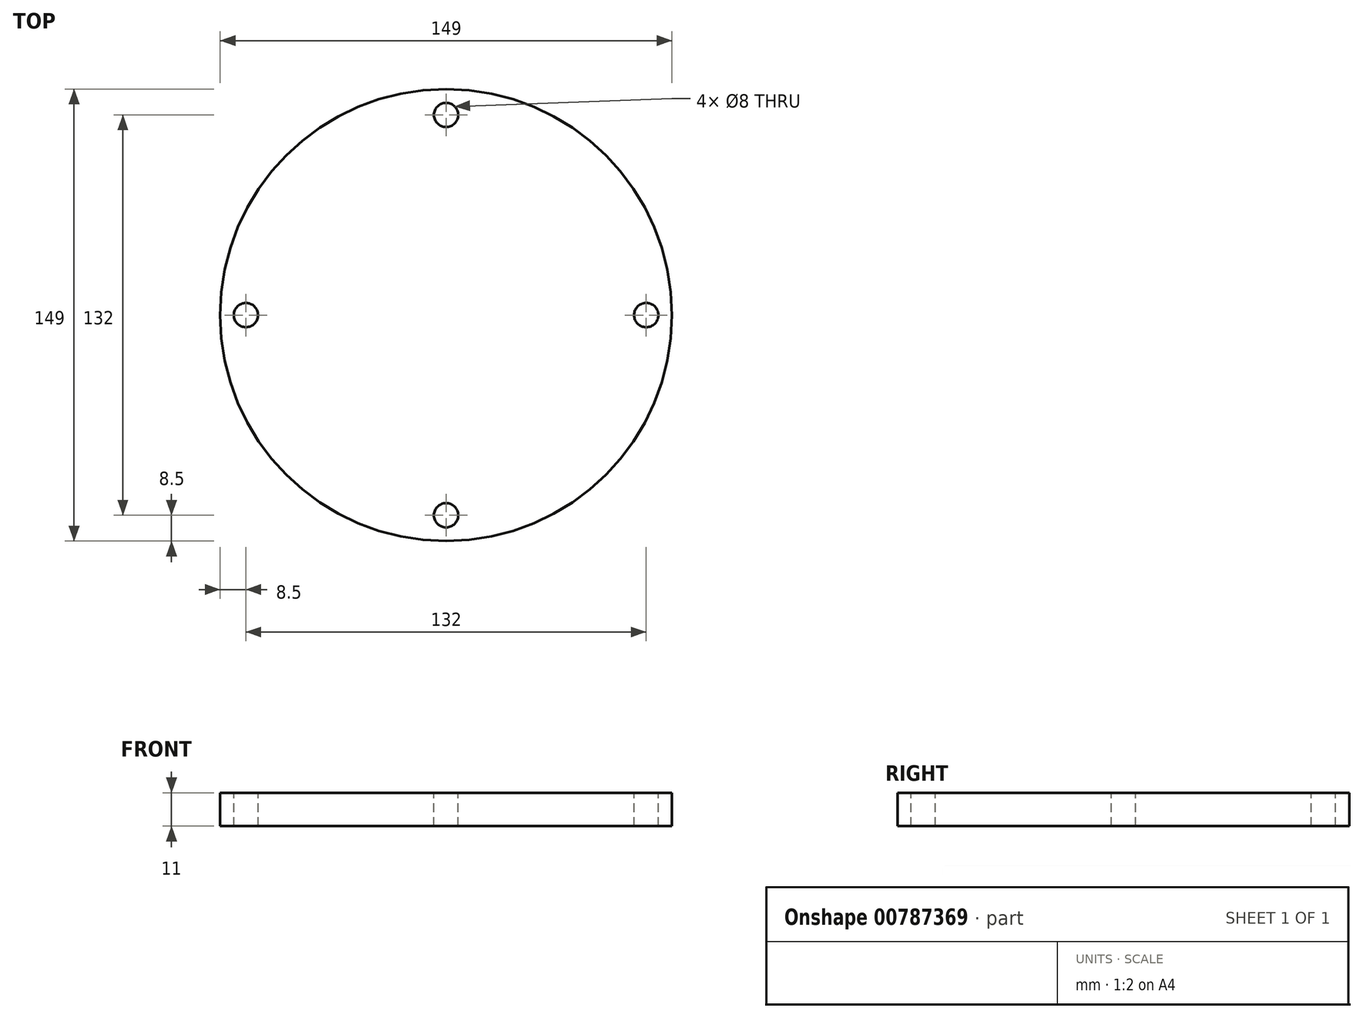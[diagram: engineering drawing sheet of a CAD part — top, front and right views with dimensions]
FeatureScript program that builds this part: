
annotation { "Feature Type Name" : "Feature", "Feature Type Description" : "" }
export const myFeature = defineFeature(function(context is Context, id is Id, definition is map)
    precondition{}
    {
        {
            var Q0;
            Q0=qCreatedBy(makeId("Top.planeOp"),FACE);
            var sketch = newSketch(context, id + "F0", { "sketchPlane" : qUnion([Q0])});
            skCircle(sketch, "E0", {"center": v(0, 0) * mm, "radius": 74.5 * mm});
            skSolve(sketch);
        }
        {
            var Q0;
            Q0=makeQuery(id+"F0.imprint","IMPRINT",FACE,{"disambiguationData":[TD([[makeQuery(id+"F0.imprint","IMPRINT",EDGE,{"derivedFrom":sQuery(id+"F0.wireOp",EDGE,"E0")}),1.0]])]});
            extrude(context, id + "F1", {"entities" : qUnion([Q0]), "depth" : 11 * mm, "offsetDistance" : 25 * mm});
        }
        {
            var Q0;
            Q0=makeQuery(id+"F1.opExtrude","CAP_FACE",FACE,{"disambiguationData":[OSD([sQuery(id+"F0.wireOp",EDGE,"E0")])],"isStart":false});
            var sketch = newSketch(context, id + "F2", { "sketchPlane" : qUnion([Q0])});
            skCircle(sketch, "E1", {"center": v(0, 0) * mm, "radius": 66 * mm});
            skSolve(sketch);
        }
        {
            var Q0;
            Q0=makeQuery(id+"F2.imprint","IMPRINT",FACE,{"disambiguationData":[TD([[makeQuery(id+"F2.imprint","IMPRINT",EDGE,{"derivedFrom":sQuery(id+"F2.wireOp",EDGE,"E1")}),1.0]])]});
            var sketch = newSketch(context, id + "F3", { "sketchPlane" : qUnion([Q0])});
            skPoint(sketch, "E2", {"position": v(-66, 0) * mm});
            skPoint(sketch, "E3", {"position": v(0, 66) * mm});
            skPoint(sketch, "E4", {"position": v(66, 0) * mm});
            skPoint(sketch, "E5", {"position": v(0, -66) * mm});
            skSolve(sketch);
        }
        {
            var Q0;
            Q0=sQuery(id+"F3.wireOp",VERTEX,"E3");
            var Q1;
            Q1=sQuery(id+"F3.wireOp",VERTEX,"E2");
            var Q2;
            Q2=sQuery(id+"F3.wireOp",VERTEX,"E4");
            var Q3;
            Q3=sQuery(id+"F3.wireOp",VERTEX,"E5");
            var Q4;
            Q4=makeQuery(id+"F1.opExtrude","SWEPT_BODY",BODY,{"disambiguationData":[OSD([sQuery(id+"F0.wireOp",EDGE,"E0")])]});
            hole(context, id + "F4", {"style" : HoleStyle.SIMPLE, "endStyle" : HoleEndStyle.THROUGH, "holeDiameter" : 8 * mm, "majorDiameter" : 5 * mm, "isTappedThrough" : true, "tappedDepth" : 12 * mm, "tapClearance" : 3, "locations" : qUnion([Q0, Q1, Q2, Q3]), "scope" : qUnion([Q4])});
        }
    });
